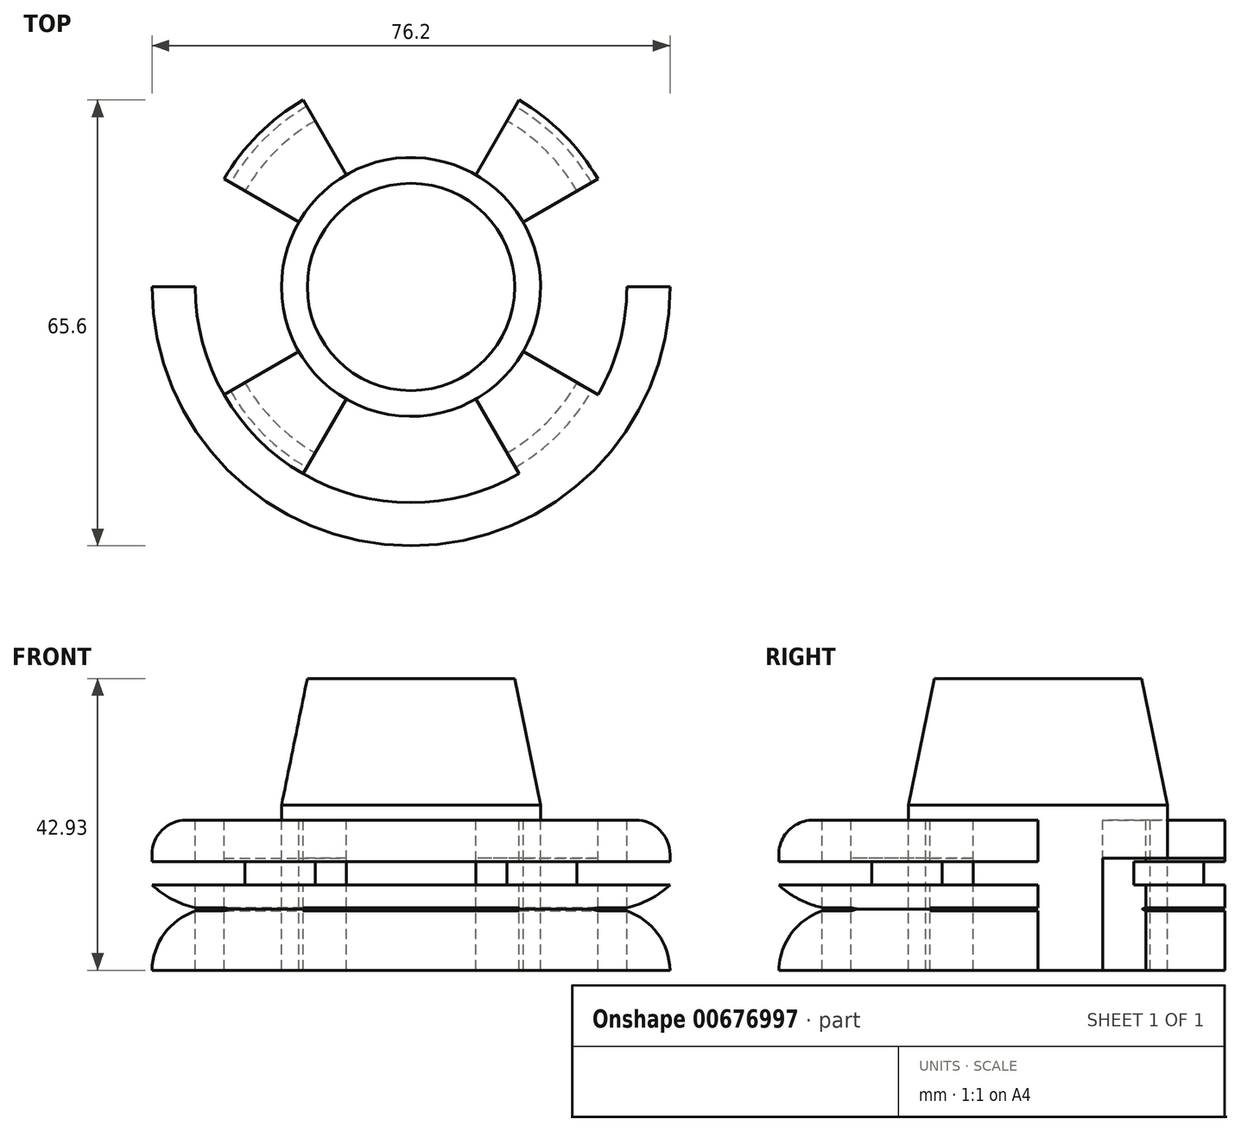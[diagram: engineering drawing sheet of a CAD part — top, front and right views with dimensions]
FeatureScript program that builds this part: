
annotation { "Feature Type Name" : "Feature", "Feature Type Description" : "" }
export const myFeature = defineFeature(function(context is Context, id is Id, definition is map)
    precondition{}
    {
        {
            var Q0;
            Q0=qCreatedBy(makeId("Top.planeOp"),FACE);
            var sketch = newSketch(context, id + "F0", { "sketchPlane" : qUnion([Q0])});
            skCircle(sketch, "E0", {"center": v(0, 0) * mm, "radius": 38.1 * mm});
            skLineSegment(sketch, "E1", {"start": v(0, 51.5) * mm, "end": v(0, -51.94) * mm});
            skLineSegment(sketch, "E2", {"start": v(-57.29, 0) * mm, "end": v(61.3, 0) * mm});
            skCircle(sketch, "E3", {"center": v(0, 0) * mm, "radius": 19.05 * mm});
            skCircle(sketch, "E4", {"center": v(0, 0) * mm, "radius": 31.75 * mm});
            skLineSegment(sketch, "E5", {"start": v(-31.75, 0) * mm, "end": v(-19.05, 0) * mm});
            skLineSegment(sketch, "E6", {"start": v(0, 31.75) * mm, "end": v(0, 19.05) * mm});
            skLineSegment(sketch, "E7", {"start": v(19.05, 0) * mm, "end": v(31.75, 0) * mm});
            skLineSegment(sketch, "E8", {"start": v(0, -19.05) * mm, "end": v(0, -31.75) * mm});
            skLineSegment(sketch, "E9.1.0", {"start": v(15.87, -27.5) * mm, "end": v(9.52, -16.5) * mm});
            skLineSegment(sketch, "E9.1.1", {"start": v(-27.5, -15.87) * mm, "end": v(-16.5, -9.52) * mm});
            skLineSegment(sketch, "E9.1.2", {"start": v(-9.52, 16.5) * mm, "end": v(-15.87, 27.5) * mm});
            skLineSegment(sketch, "E9.1.3", {"start": v(16.5, 9.52) * mm, "end": v(27.5, 15.87) * mm});
            skLineSegment(sketch, "E9.2.0", {"start": v(15.88, 27.5) * mm, "end": v(9.53, 16.5) * mm});
            skLineSegment(sketch, "E9.2.1", {"start": v(27.5, -15.88) * mm, "end": v(16.5, -9.53) * mm});
            skLineSegment(sketch, "E9.2.2", {"start": v(-9.53, -16.5) * mm, "end": v(-15.88, -27.5) * mm});
            skLineSegment(sketch, "E9.2.3", {"start": v(-16.5, 9.53) * mm, "end": v(-27.5, 15.88) * mm});
            skSolve(sketch);
        }
        {
            var Q0;
            {var subQ1=sQuery(id+"F0.wireOp",EDGE,"E2");var subQ3=sQuery(id+"F0.wireOp",EDGE,"E0");var subQ4=makeQuery(id+"F0.imprint","INTERSECT",VERTEX,{"disambiguationData":[OD(0.0)],"derivedFrom":[subQ3,subQ1]});Q0=makeQuery(id+"F0.imprint","IMPRINT",FACE,{"disambiguationData":[TD([[makeQuery(id+"F0.imprint","IMPRINT",EDGE,{"disambiguationData":[TD([[subQ4,1.0]])],"derivedFrom":subQ3}),1.0]])]});}
            var Q1;
            {var subQ3=sQuery(id+"F0.wireOp",EDGE,"E0");var subQ5=sQuery(id+"F0.wireOp",EDGE,"E1");var subQ6=makeQuery(id+"F0.imprint","INTERSECT",VERTEX,{"disambiguationData":[OD(0.0)],"derivedFrom":[subQ3,subQ5]});Q1=makeQuery(id+"F0.imprint","IMPRINT",FACE,{"disambiguationData":[TD([[makeQuery(id+"F0.imprint","IMPRINT",EDGE,{"disambiguationData":[TD([[subQ6,1.0]])],"derivedFrom":subQ3}),1.0]])]});}
            var Q2;
            {var subQ1=sQuery(id+"F0.wireOp",EDGE,"E2");var subQ4=sQuery(id+"F0.wireOp",EDGE,"E0");var subQ5=makeQuery(id+"F0.imprint","INTERSECT",VERTEX,{"disambiguationData":[OD(1.0)],"derivedFrom":[subQ4,subQ1]});Q2=makeQuery(id+"F0.imprint","IMPRINT",FACE,{"disambiguationData":[TD([[makeQuery(id+"F0.imprint","IMPRINT",EDGE,{"disambiguationData":[TD([[subQ5,-1.0]])],"derivedFrom":subQ4}),1.0]])]});}
            var Q3;
            {var subQ1=sQuery(id+"F0.wireOp",EDGE,"E1");var subQ6=sQuery(id+"F0.wireOp",EDGE,"E0");var subQ8=makeQuery(id+"F0.imprint","INTERSECT",VERTEX,{"disambiguationData":[OD(0.0)],"derivedFrom":[subQ6,subQ1]});Q3=makeQuery(id+"F0.imprint","IMPRINT",FACE,{"disambiguationData":[TD([[makeQuery(id+"F0.imprint","IMPRINT",EDGE,{"disambiguationData":[TD([[subQ8,-1.0]])],"derivedFrom":subQ6}),1.0]])]});}
            var Q4;
            {var subQ0=sQuery(id+"F0.wireOp",EDGE,"E3");var subQ1=makeQuery(id+"F0.imprint","INTERSECT",VERTEX,{"derivedFrom":[subQ0,sQuery(id+"F0.wireOp",EDGE,"E9.1.2")]});Q4=makeQuery(id+"F0.imprint","IMPRINT",FACE,{"disambiguationData":[TD([[makeQuery(id+"F0.imprint","IMPRINT",EDGE,{"disambiguationData":[TD([[subQ1,-1.0]])],"derivedFrom":subQ0}),1.0]])]});}
            var Q5;
            {var subQ0=sQuery(id+"F0.wireOp",EDGE,"E3");var subQ1=makeQuery(id+"F0.imprint","INTERSECT",VERTEX,{"derivedFrom":[subQ0,sQuery(id+"F0.wireOp",EDGE,"E9.1.3")]});Q5=makeQuery(id+"F0.imprint","IMPRINT",FACE,{"disambiguationData":[TD([[makeQuery(id+"F0.imprint","IMPRINT",EDGE,{"disambiguationData":[TD([[subQ1,-1.0]])],"derivedFrom":subQ0}),1.0]])]});}
            var Q6;
            {var subQ0=sQuery(id+"F0.wireOp",EDGE,"E3");var subQ1=makeQuery(id+"F0.imprint","INTERSECT",VERTEX,{"derivedFrom":[subQ0,sQuery(id+"F0.wireOp",EDGE,"E9.1.0")]});Q6=makeQuery(id+"F0.imprint","IMPRINT",FACE,{"disambiguationData":[TD([[makeQuery(id+"F0.imprint","IMPRINT",EDGE,{"disambiguationData":[TD([[subQ1,-1.0]])],"derivedFrom":subQ0}),1.0]])]});}
            var Q7;
            {var subQ0=sQuery(id+"F0.wireOp",EDGE,"E3");var subQ3=makeQuery(id+"F0.imprint","INTERSECT",VERTEX,{"derivedFrom":[subQ0,sQuery(id+"F0.wireOp",EDGE,"E9.1.1")]});Q7=makeQuery(id+"F0.imprint","IMPRINT",FACE,{"disambiguationData":[TD([[makeQuery(id+"F0.imprint","IMPRINT",EDGE,{"disambiguationData":[TD([[subQ3,-1.0]])],"derivedFrom":subQ0}),1.0]])]});}
            var Q8;
            {var subQ0=sQuery(id+"F0.wireOp",EDGE,"E5");Q8=makeQuery(id+"F0.imprint","IMPRINT",FACE,{"disambiguationData":[TD([[makeQuery(id+"F0.imprint","IMPRINT",EDGE,{"derivedFrom":subQ0}),-1.0]])]});}
            var Q9;
            {var subQ0=sQuery(id+"F0.wireOp",EDGE,"E9.1.1");Q9=makeQuery(id+"F0.imprint","IMPRINT",FACE,{"disambiguationData":[TD([[makeQuery(id+"F0.imprint","IMPRINT",EDGE,{"derivedFrom":subQ0}),-1.0]])]});}
            var Q10;
            {var subQ0=sQuery(id+"F0.wireOp",EDGE,"E8");Q10=makeQuery(id+"F0.imprint","IMPRINT",FACE,{"disambiguationData":[TD([[makeQuery(id+"F0.imprint","IMPRINT",EDGE,{"derivedFrom":subQ0}),-1.0]])]});}
            var Q11;
            {var subQ0=sQuery(id+"F0.wireOp",EDGE,"E8");Q11=makeQuery(id+"F0.imprint","IMPRINT",FACE,{"disambiguationData":[TD([[makeQuery(id+"F0.imprint","IMPRINT",EDGE,{"derivedFrom":subQ0}),1.0]])]});}
            var Q12;
            {var subQ0=sQuery(id+"F0.wireOp",EDGE,"E9.1.0");Q12=makeQuery(id+"F0.imprint","IMPRINT",FACE,{"disambiguationData":[TD([[makeQuery(id+"F0.imprint","IMPRINT",EDGE,{"derivedFrom":subQ0}),-1.0]])]});}
            var Q13;
            {var subQ0=sQuery(id+"F0.wireOp",EDGE,"E7");Q13=makeQuery(id+"F0.imprint","IMPRINT",FACE,{"disambiguationData":[TD([[makeQuery(id+"F0.imprint","IMPRINT",EDGE,{"derivedFrom":subQ0}),-1.0]])]});}
            var Q14;
            {var subQ0=sQuery(id+"F0.wireOp",EDGE,"E7");Q14=makeQuery(id+"F0.imprint","IMPRINT",FACE,{"disambiguationData":[TD([[makeQuery(id+"F0.imprint","IMPRINT",EDGE,{"derivedFrom":subQ0}),1.0]])]});}
            var Q15;
            {var subQ0=sQuery(id+"F0.wireOp",EDGE,"E9.1.3");Q15=makeQuery(id+"F0.imprint","IMPRINT",FACE,{"disambiguationData":[TD([[makeQuery(id+"F0.imprint","IMPRINT",EDGE,{"derivedFrom":subQ0}),1.0]])]});}
            var Q16;
            {var subQ0=sQuery(id+"F0.wireOp",EDGE,"E6");Q16=makeQuery(id+"F0.imprint","IMPRINT",FACE,{"disambiguationData":[TD([[makeQuery(id+"F0.imprint","IMPRINT",EDGE,{"derivedFrom":subQ0}),1.0]])]});}
            var Q17;
            {var subQ0=sQuery(id+"F0.wireOp",EDGE,"E9.1.2");Q17=makeQuery(id+"F0.imprint","IMPRINT",FACE,{"disambiguationData":[TD([[makeQuery(id+"F0.imprint","IMPRINT",EDGE,{"derivedFrom":subQ0}),1.0]])]});}
            var Q18;
            {var subQ0=sQuery(id+"F0.wireOp",EDGE,"E5");Q18=makeQuery(id+"F0.imprint","IMPRINT",FACE,{"disambiguationData":[TD([[makeQuery(id+"F0.imprint","IMPRINT",EDGE,{"derivedFrom":subQ0}),1.0]])]});}
            var Q19;
            {var subQ0=sQuery(id+"F0.wireOp",EDGE,"E6");Q19=makeQuery(id+"F0.imprint","IMPRINT",FACE,{"disambiguationData":[TD([[makeQuery(id+"F0.imprint","IMPRINT",EDGE,{"derivedFrom":subQ0}),-1.0]])]});}
            extrude(context, id + "F1", {"entities" : qUnion([Q0, Q1, Q2, Q3, Q4, Q5, Q6, Q7, Q8, Q9, Q10, Q11, Q12, Q13, Q14, Q15, Q16, Q17, Q18, Q19]), "oppositeDirection" : true, "depth" : 22.1 * mm, "offsetDistance" : 25.4 * mm});
        }
        {
            var Q0;
            {var subQ0=sQuery(id+"F0.wireOp",EDGE,"E3");var subQ1=makeQuery(id+"F0.imprint","INTERSECT",VERTEX,{"derivedFrom":[subQ0,sQuery(id+"F0.wireOp",EDGE,"E9.1.2")]});Q0=makeQuery(id+"F0.imprint","IMPRINT",FACE,{"disambiguationData":[TD([[makeQuery(id+"F0.imprint","IMPRINT",EDGE,{"disambiguationData":[TD([[subQ1,-1.0]])],"derivedFrom":subQ0}),1.0]])]});}
            var Q1;
            {var subQ0=sQuery(id+"F0.wireOp",EDGE,"E3");var subQ1=makeQuery(id+"F0.imprint","INTERSECT",VERTEX,{"derivedFrom":[subQ0,sQuery(id+"F0.wireOp",EDGE,"E9.1.3")]});Q1=makeQuery(id+"F0.imprint","IMPRINT",FACE,{"disambiguationData":[TD([[makeQuery(id+"F0.imprint","IMPRINT",EDGE,{"disambiguationData":[TD([[subQ1,-1.0]])],"derivedFrom":subQ0}),1.0]])]});}
            var Q2;
            {var subQ0=sQuery(id+"F0.wireOp",EDGE,"E3");var subQ1=makeQuery(id+"F0.imprint","INTERSECT",VERTEX,{"derivedFrom":[subQ0,sQuery(id+"F0.wireOp",EDGE,"E9.1.0")]});Q2=makeQuery(id+"F0.imprint","IMPRINT",FACE,{"disambiguationData":[TD([[makeQuery(id+"F0.imprint","IMPRINT",EDGE,{"disambiguationData":[TD([[subQ1,-1.0]])],"derivedFrom":subQ0}),1.0]])]});}
            var Q3;
            {var subQ0=sQuery(id+"F0.wireOp",EDGE,"E3");var subQ3=makeQuery(id+"F0.imprint","INTERSECT",VERTEX,{"derivedFrom":[subQ0,sQuery(id+"F0.wireOp",EDGE,"E9.1.1")]});Q3=makeQuery(id+"F0.imprint","IMPRINT",FACE,{"disambiguationData":[TD([[makeQuery(id+"F0.imprint","IMPRINT",EDGE,{"disambiguationData":[TD([[subQ3,-1.0]])],"derivedFrom":subQ0}),1.0]])]});}
            extrude(context, id + "F2", {"entities" : qUnion([Q0, Q1, Q2, Q3]), "operationType" : NewBodyOperationType.ADD, "depth" : 20.83 * mm, "offsetDistance" : 25.4 * mm});
        }
        {
            var Q0;
            Q0=makeQuery(id+"F1.opExtrude","CAP_EDGE",EDGE,{"disambiguationData":[OSD([sQuery(id+"F0.wireOp",EDGE,"E0")])],"isStart":true});
            fillet(context, id + "F3", {"entities" : qUnion([Q0]), "radius" : 5.08 * mm, "tangentPropagation" : true, "allowEdgeOverflow" : false});
        }
        {
            var Q0;
            {var subQ0=sQuery(id+"F0.wireOp",EDGE,"E5");Q0=makeQuery(id+"F0.imprint","IMPRINT",FACE,{"disambiguationData":[TD([[makeQuery(id+"F0.imprint","IMPRINT",EDGE,{"derivedFrom":subQ0}),1.0]])]});}
            var Q1;
            {var subQ0=sQuery(id+"F0.wireOp",EDGE,"E6");Q1=makeQuery(id+"F0.imprint","IMPRINT",FACE,{"disambiguationData":[TD([[makeQuery(id+"F0.imprint","IMPRINT",EDGE,{"derivedFrom":subQ0}),-1.0]])]});}
            var Q2;
            {var subQ0=sQuery(id+"F0.wireOp",EDGE,"E9.1.3");Q2=makeQuery(id+"F0.imprint","IMPRINT",FACE,{"disambiguationData":[TD([[makeQuery(id+"F0.imprint","IMPRINT",EDGE,{"derivedFrom":subQ0}),1.0]])]});}
            var Q3;
            {var subQ0=sQuery(id+"F0.wireOp",EDGE,"E7");Q3=makeQuery(id+"F0.imprint","IMPRINT",FACE,{"disambiguationData":[TD([[makeQuery(id+"F0.imprint","IMPRINT",EDGE,{"derivedFrom":subQ0}),-1.0]])]});}
            var Q4;
            {var subQ0=sQuery(id+"F0.wireOp",EDGE,"E8");Q4=makeQuery(id+"F0.imprint","IMPRINT",FACE,{"disambiguationData":[TD([[makeQuery(id+"F0.imprint","IMPRINT",EDGE,{"derivedFrom":subQ0}),1.0]])]});}
            var Q5;
            {var subQ0=sQuery(id+"F0.wireOp",EDGE,"E9.1.1");Q5=makeQuery(id+"F0.imprint","IMPRINT",FACE,{"disambiguationData":[TD([[makeQuery(id+"F0.imprint","IMPRINT",EDGE,{"derivedFrom":subQ0}),-1.0]])]});}
            extrude(context, id + "F4", {"entities" : qUnion([Q0, Q1, Q2, Q3, Q4, Q5]), "operationType" : NewBodyOperationType.REMOVE, "oppositeDirection" : true, "depth" : 5.6 * mm, "offsetDistance" : 25.4 * mm});
        }
        {
            var Q0;
            Q0=qCreatedBy(makeId("Top.planeOp"),FACE);
            var sketch = newSketch(context, id + "F5", { "sketchPlane" : qUnion([Q0])});
            skCircle(sketch, "E10", {"center": v(0, 0) * mm, "radius": 18.73 * mm});
            skSolve(sketch);
        }
        {
            var Q0;
            Q0=qCreatedBy(makeId("Front.planeOp"),FACE);
            var sketch = newSketch(context, id + "F6", { "sketchPlane" : qUnion([Q0])});
            skLineSegment(sketch, "E11", {"start": v(19.5, 20.83) * mm, "end": v(19.5, 0) * mm});
            skLineSegment(sketch, "E12", {"start": v(19.5, 0) * mm, "end": v(15.25, 20.83) * mm});
            skLineSegment(sketch, "E13", {"start": v(15.25, 20.83) * mm, "end": v(19.5, 20.83) * mm});
            skSolve(sketch);
        }
        {
            var Q0;
            Q0=makeQuery(id+"F6.imprint","IMPRINT",FACE,{"disambiguationData":[TD([[makeQuery(id+"F6.imprint","IMPRINT",EDGE,{"derivedFrom":sQuery(id+"F6.wireOp",EDGE,"E11")}),-1.0]])]});
            var Q1;
            Q1=makeQuery(id+"F2.opExtrude","CAP_EDGE",EDGE,{"disambiguationData":[OSD([sQuery(id+"F0.wireOp",EDGE,"E3")])],"isStart":false});
            revolve(context, id + "F7", {"operationType" : NewBodyOperationType.REMOVE, "entities" : qUnion([Q0]), "axis" : qUnion([Q1]), "revolveType" : RevolveType.FULL, "oppositeDirection" : true});
        }
        {
            var Q0;
            Q0=qCreatedBy(makeId("Front.planeOp"),FACE);
            var sketch = newSketch(context, id + "F8", { "sketchPlane" : qUnion([Q0])});
            skLineSegment(sketch, "E14", {"start": v(-38.1, -22.27) * mm, "end": v(-38.1, 0) * mm});
            skLineSegment(sketch, "E15.bottom", {"start": v(-38.1, -6.1) * mm, "end": v(-28.2, -6.1) * mm});
            skLineSegment(sketch, "E15.top", {"start": v(-38.1, -9.55) * mm, "end": v(-28.2, -9.55) * mm});
            skLineSegment(sketch, "E15.left", {"start": v(-38.1, -6.1) * mm, "end": v(-38.1, -9.55) * mm});
            skLineSegment(sketch, "E15.right", {"start": v(-28.2, -6.1) * mm, "end": v(-28.2, -9.55) * mm});
            skArc(sketch, "E16", {"start": v(-38.1, -9.55) * mm, "mid": v(-34.65, -11.9) * mm, "end": v(-30.66, -13.1) * mm});
            skArc(sketch, "E17", {"start": v(-30.66, -13.1) * mm, "mid": v(-36, -16.36) * mm, "end": v(-38.1, -22.27) * mm});
            skSolve(sketch);
        }
        {
            var Q0;
            Q0=makeQuery(id+"F8.imprint","IMPRINT",FACE,{"disambiguationData":[TD([[makeQuery(id+"F8.imprint","IMPRINT",EDGE,{"derivedFrom":sQuery(id+"F8.wireOp",EDGE,"E15.bottom")}),-1.0]])]});
            var Q1;
            {var subQ2=sQuery(id+"F8.wireOp",EDGE,"E16");Q1=makeQuery(id+"F8.imprint","IMPRINT",FACE,{"disambiguationData":[TD([[makeQuery(id+"F8.imprint","IMPRINT",EDGE,{"derivedFrom":subQ2}),-1.0]])]});}
            var Q2;
            {var subQ0=sQuery(id+"F0.wireOp",EDGE,"E0");Q2=makeQuery(id+"F3.opFillet","BLEND_EDGE",EDGE,{"blendedFrom":[makeQuery(id+"F1.opExtrude","CAP_EDGE",EDGE,{"disambiguationData":[OSD([subQ0])],"isStart":true}),makeQuery(id+"F1.opExtrude","SWEPT_FACE",FACE,{"disambiguationData":[OSD([subQ0])]})],"blendedInto":[makeQuery(id+"F1.opExtrude","SWEPT_FACE",FACE,{"disambiguationData":[OSD([subQ0])]})]});}
            revolve(context, id + "F9", {"operationType" : NewBodyOperationType.REMOVE, "entities" : qUnion([Q0, Q1]), "axis" : qUnion([Q2]), "revolveType" : RevolveType.FULL, "oppositeDirection" : true});
        }
    });
